# Revit family: D5X-ELE_2014
name_source: partatom
category: Specialty Equipment
revit_build: Autodesk Revit 2014 (Build: 20130308_1515(x64)
units: mm (PartAtom-declared; Revit-internal decimal feet)

## types (1)
- 89 1/2" (7'-5 1/2") Length
    Back Clearance = 3"
    Bumper = Extruded PVC - 739 Royal Blue
    Case = Textured Sheet Metal (Steel Painted) - 149 White Satin Matte
    Case Interior - Back Panel = Mirror
    Case Interior - Side Panel = Sheet Metal (Steel Painted) - 700 Interior White
    Case Weight = 1200.00 lbf
    Close Off Panel = Textured Sheet Metal (Steel Painted) - 701 Black
    Cutsheet URL = http://www.hussmann.com
    Depth = 42"
    Description = Multi-Deck Dairy​ & Delicatessen End Case
    End Weight = 0.00 lbf
    Ends = Textured Sheet Metal (Steel Painted) - 149 White Satin Matte
    Glazing = Glass
    Height = 81 3/4"
    Manufacturer = Hussmann Corporation
    Manufacturer Disclaimer = The information in this file is not intended to be an exact representation of the corresponding Hussmann product.  Further, we reserve the right to change or revise specifications and product design in connection with any feature of our products. Such changes do not entitle the buyer to corresponding changes, improvements, additions, or replacements for equipment previously sold or shipped.
    Model = D5X-ELE
    Model URL = http://www.hussmann.com
    Note from Manufacturer = This model only comes in this length.
    Number of Shelves = 4
    Number of Supports = 3
    Refrig. Liquid = Liquid
    Refrig. Suction = Suction
    Refrigeration Lines Liquid = 3/8"
    Refrigeration Lines Suction = 7/8"
    Revit Family Date = 08/31/2015
    Shelves = Sheet Metal (Steel Painted) - 700 Interior White
    Splashguard = Textured Sheet Metal (Steel Painted) - 701 Black
    Top Clearance = 3"
    Total Weight = 1200.00 lbf
    Type Comments = Excel
    URL = www.hussmann.com
    Waste Drain = 1 1/4"
    Width = 89 1/2"

## geometry (parser evidence)
native form markers: Sweep x14
no freeform markers — native parametric forms only
